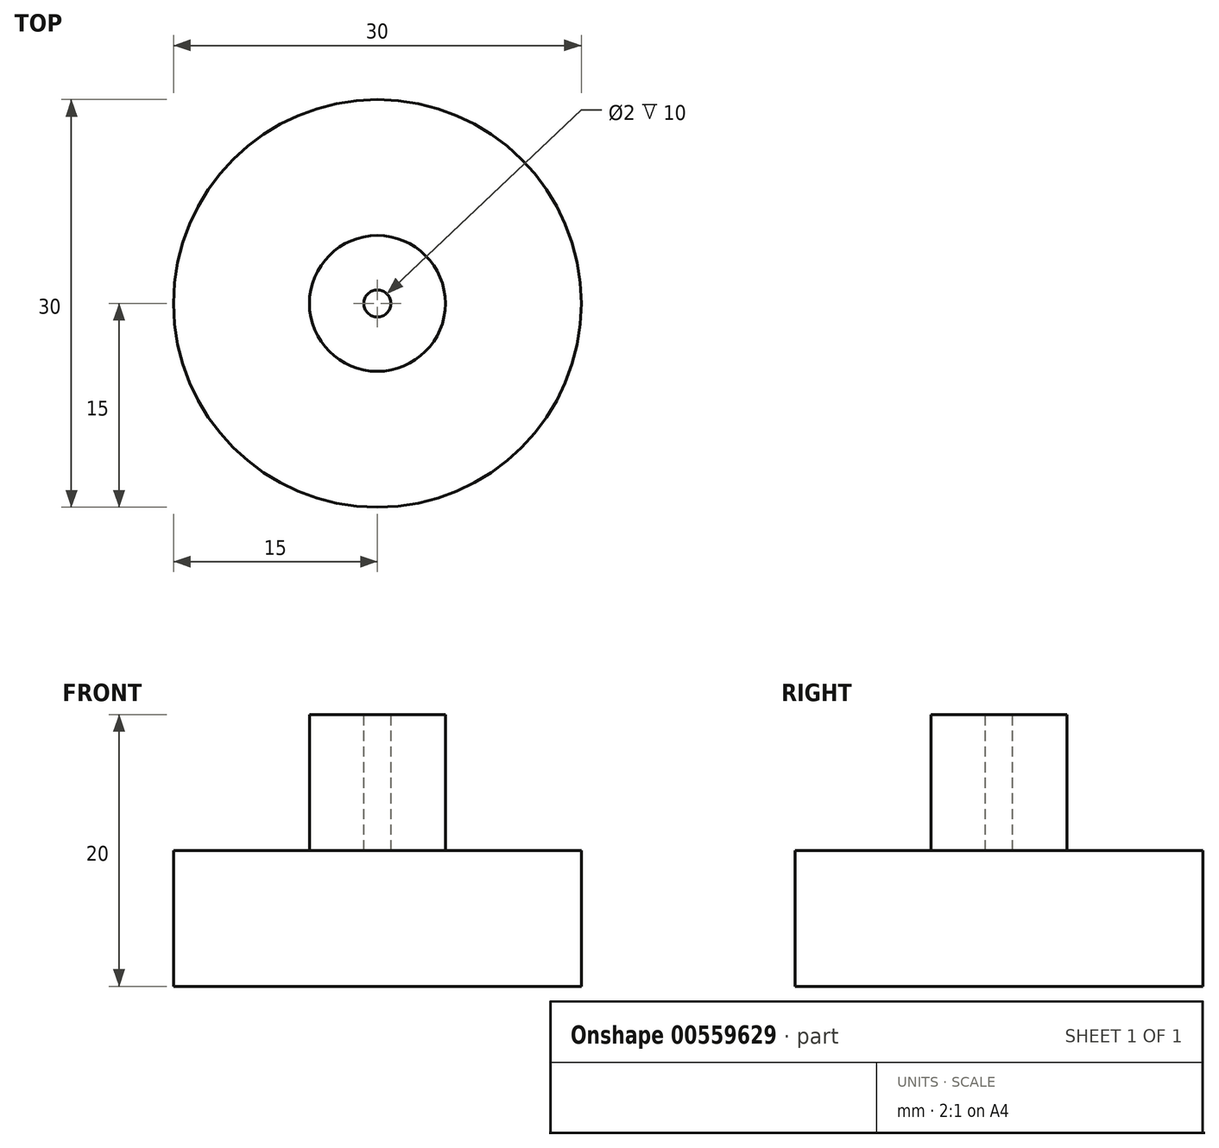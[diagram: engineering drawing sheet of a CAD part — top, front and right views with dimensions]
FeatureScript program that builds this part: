
annotation { "Feature Type Name" : "Feature", "Feature Type Description" : "" }
export const myFeature = defineFeature(function(context is Context, id is Id, definition is map)
    precondition{}
    {
        {
            var Q0;
            Q0=qCreatedBy(makeId("Top.planeOp"),FACE);
            var sketch = newSketch(context, id + "F0", { "sketchPlane" : qUnion([Q0])});
            skCircle(sketch, "E0", {"center": v(0, 0) * mm, "radius": 15 * mm});
            skSolve(sketch);
        }
        {
            var Q0;
            Q0=makeQuery(id+"F0.imprint","IMPRINT",FACE,{"disambiguationData":[TD([[makeQuery(id+"F0.imprint","IMPRINT",EDGE,{"derivedFrom":sQuery(id+"F0.wireOp",EDGE,"E0")}),1.0]])]});
            extrude(context, id + "F1", {"entities" : qUnion([Q0]), "depth" : 10 * mm, "offsetDistance" : 25 * mm});
        }
        {
            var Q0;
            Q0=makeQuery(id+"F1.opExtrude","CAP_FACE",FACE,{"disambiguationData":[OSD([sQuery(id+"F0.wireOp",EDGE,"E0")])],"isStart":false});
            var sketch = newSketch(context, id + "F2", { "sketchPlane" : qUnion([Q0])});
            skCircle(sketch, "E1", {"center": v(0, 0) * mm, "radius": 5 * mm});
            skSolve(sketch);
        }
        {
            var Q0;
            Q0 = qSketchRegion(id + "F2", true);
            extrude(context, id + "F3", {"entities" : qUnion([Q0]), "operationType" : NewBodyOperationType.ADD, "depth" : 10 * mm, "offsetDistance" : 25 * mm});
        }
        {
            var Q0;
            Q0=makeQuery(id+"F3.opExtrude","CAP_FACE",FACE,{"disambiguationData":[OSD([sQuery(id+"F2.wireOp",EDGE,"E1")])],"isStart":false});
            var sketch = newSketch(context, id + "F4", { "sketchPlane" : qUnion([Q0])});
            skCircle(sketch, "E2", {"center": v(0, 0) * mm, "radius": 1 * mm});
            skSolve(sketch);
        }
        {
            var Q0;
            Q0 = qSketchRegion(id + "F4", true);
            extrude(context, id + "F5", {"entities" : qUnion([Q0]), "operationType" : NewBodyOperationType.REMOVE, "oppositeDirection" : true, "depth" : 10 * mm, "offsetDistance" : 25 * mm});
        }
    });
